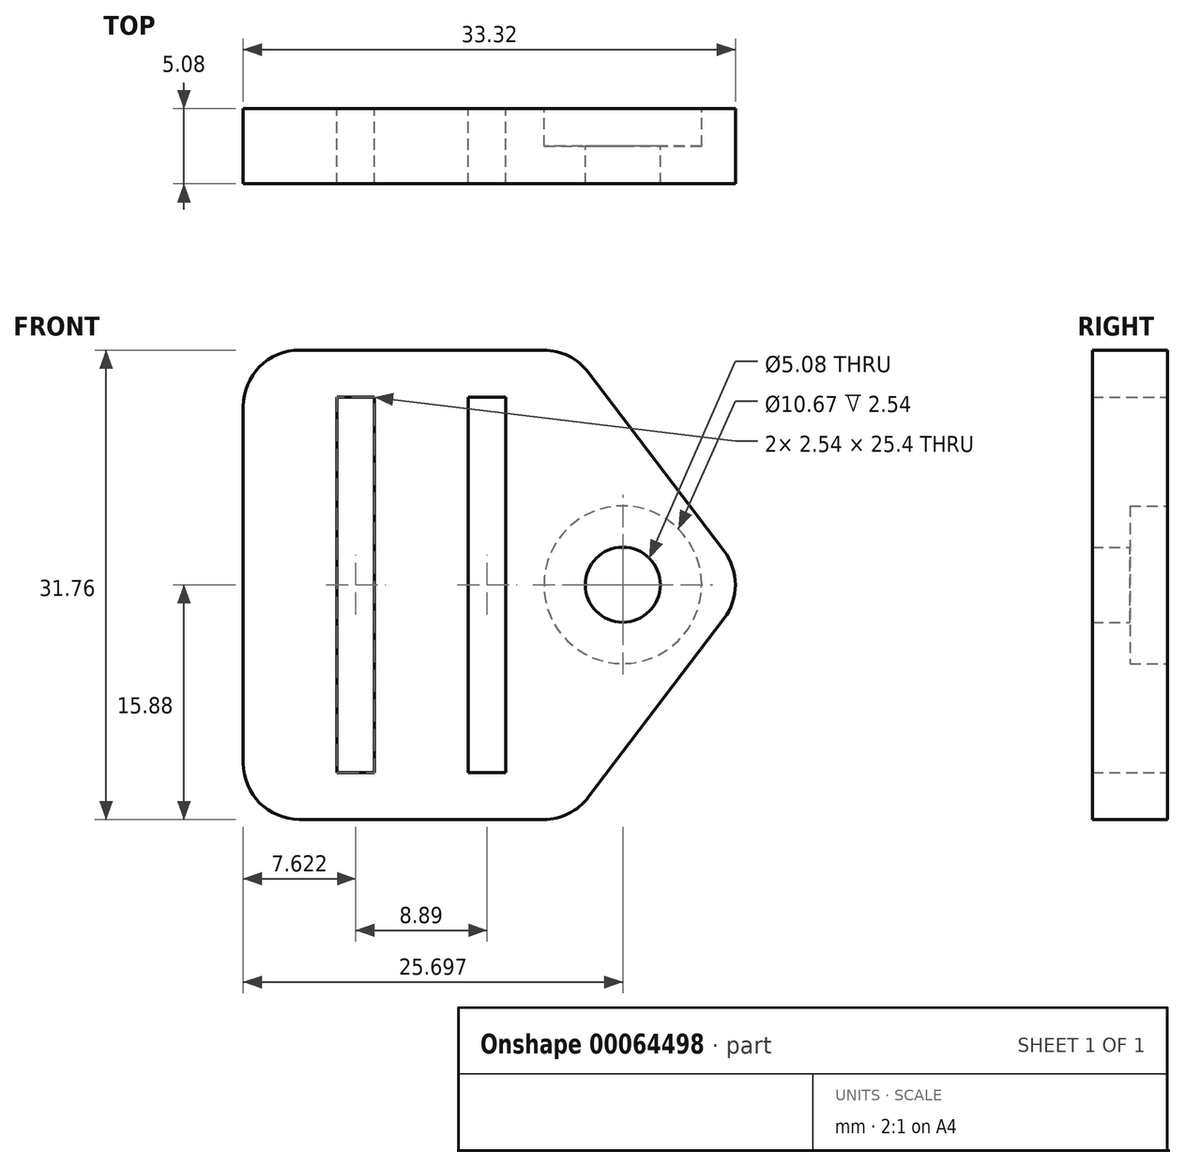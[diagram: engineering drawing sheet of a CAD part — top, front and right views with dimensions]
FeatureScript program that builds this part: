
annotation { "Feature Type Name" : "Feature", "Feature Type Description" : "" }
export const myFeature = defineFeature(function(context is Context, id is Id, definition is map)
    precondition{}
    {
        {
            var Q0;
            Q0=qCreatedBy(makeId("Front.planeOp"),FACE);
            var sketch = newSketch(context, id + "F0", { "sketchPlane" : qUnion([Q0])});
            skLineSegment(sketch, "E0", {"start": v(-37.2, 12.06) * mm, "end": v(-37.2, -12.07) * mm});
            skLineSegment(sketch, "E1", {"start": v(-33.4, -15.88) * mm, "end": v(-16.87, -15.88) * mm});
            skLineSegment(sketch, "E2", {"start": v(-13.84, -14.37) * mm, "end": v(-4.67, -2.3) * mm});
            skLineSegment(sketch, "E3", {"start": v(-4.67, 2.3) * mm, "end": v(-13.84, 14.37) * mm});
            skLineSegment(sketch, "E4", {"start": v(-16.87, 15.88) * mm, "end": v(-33.4, 15.88) * mm});
            skPoint(sketch, "E5.visualSharp", {"position": v(-37.2, 15.87) * mm});
            skArc(sketch, "E5.filletArc", {"start": v(-33.4, 15.87) * mm, "mid": v(-36.1, 14.76) * mm, "end": v(-37.2, 12.06) * mm});
            skPoint(sketch, "E6.visualSharp", {"position": v(-14.98, 15.88) * mm});
            skArc(sketch, "E6.filletArc", {"start": v(-13.84, 14.37) * mm, "mid": v(-15.18, 15.48) * mm, "end": v(-16.87, 15.88) * mm});
            skPoint(sketch, "E7.visualSharp", {"position": v(-37.2, -15.88) * mm});
            skArc(sketch, "E7.filletArc", {"start": v(-37.2, -12.07) * mm, "mid": v(-36.1, -14.76) * mm, "end": v(-33.4, -15.88) * mm});
            skPoint(sketch, "E8.visualSharp", {"position": v(-14.98, -15.88) * mm});
            skArc(sketch, "E8.filletArc", {"start": v(-16.87, -15.88) * mm, "mid": v(-15.18, -15.48) * mm, "end": v(-13.84, -14.37) * mm});
            skPoint(sketch, "E9.visualSharp", {"position": v(-2.92, 0) * mm});
            skArc(sketch, "E9.filletArc", {"start": v(-4.67, -2.3) * mm, "mid": v(-3.9, 0) * mm, "end": v(-4.67, 2.3) * mm});
            skLineSegment(sketch, "E10", {"start": v(-37.2, 0) * mm, "end": v(-2.92, 0) * mm});
            skLineSegment(sketch, "E11.bottom", {"start": v(-28.32, -12.7) * mm, "end": v(-30.86, -12.7) * mm});
            skLineSegment(sketch, "E11.top", {"start": v(-28.32, 12.7) * mm, "end": v(-30.86, 12.7) * mm});
            skLineSegment(sketch, "E11.left", {"start": v(-28.32, -12.7) * mm, "end": v(-28.32, 12.7) * mm});
            skLineSegment(sketch, "E11.right", {"start": v(-30.86, -12.7) * mm, "end": v(-30.86, 12.7) * mm});
            skPoint(sketch, "E11.middle", {"position": v(-29.59, 0) * mm});
            skLineSegment(sketch, "E12.bottom", {"start": v(-19.43, -12.7) * mm, "end": v(-21.97, -12.7) * mm});
            skLineSegment(sketch, "E12.top", {"start": v(-19.43, 12.7) * mm, "end": v(-21.97, 12.7) * mm});
            skLineSegment(sketch, "E12.left", {"start": v(-19.43, -12.7) * mm, "end": v(-19.43, 12.7) * mm});
            skLineSegment(sketch, "E12.right", {"start": v(-21.97, -12.7) * mm, "end": v(-21.97, 12.7) * mm});
            skPoint(sketch, "E12.middle", {"position": v(-20.7, 0) * mm});
            skCircle(sketch, "E13", {"center": v(-11.51, 0) * mm, "radius": 2.54 * mm});
            skSolve(sketch);
        }
        {
            var Q0;
            {var subQ1=sQuery(id+"F0.wireOp",EDGE,"E3");Q0=makeQuery(id+"F0.imprint","IMPRINT",FACE,{"disambiguationData":[TD([[makeQuery(id+"F0.imprint","IMPRINT",EDGE,{"derivedFrom":subQ1}),1.0]])]});}
            var Q1;
            Q1=makeQuery(id+"F0.imprint","IMPRINT",FACE,{"disambiguationData":[TD([[makeQuery(id+"F0.imprint","IMPRINT",EDGE,{"derivedFrom":sQuery(id+"F0.wireOp",EDGE,"E1")}),1.0]])]});
            extrude(context, id + "F1", {"entities" : qUnion([Q0, Q1]), "depth" : 5.08 * mm});
        }
        {
            var Q0;
            Q0=makeQuery(id+"F1.opExtrude","CAP_FACE",FACE,{"disambiguationData":[OSD([sQuery(id+"F0.wireOp",EDGE,"E0"),sQuery(id+"F0.wireOp",EDGE,"E1"),sQuery(id+"F0.wireOp",EDGE,"E2"),sQuery(id+"F0.wireOp",EDGE,"E3"),sQuery(id+"F0.wireOp",EDGE,"E4"),sQuery(id+"F0.wireOp",EDGE,"E5.filletArc"),sQuery(id+"F0.wireOp",EDGE,"E6.filletArc"),sQuery(id+"F0.wireOp",EDGE,"E7.filletArc"),sQuery(id+"F0.wireOp",EDGE,"E8.filletArc"),sQuery(id+"F0.wireOp",EDGE,"E9.filletArc"),sQuery(id+"F0.wireOp",EDGE,"E11.bottom"),sQuery(id+"F0.wireOp",EDGE,"E11.top"),sQuery(id+"F0.wireOp",EDGE,"E11.left"),sQuery(id+"F0.wireOp",EDGE,"E11.right"),sQuery(id+"F0.wireOp",EDGE,"E12.bottom"),sQuery(id+"F0.wireOp",EDGE,"E12.top"),sQuery(id+"F0.wireOp",EDGE,"E12.left"),sQuery(id+"F0.wireOp",EDGE,"E12.right"),sQuery(id+"F0.wireOp",EDGE,"E13")])],"isStart":true});
            var sketch = newSketch(context, id + "F2", { "sketchPlane" : qUnion([Q0])});
            skCircle(sketch, "E14", {"center": v(11.51, 0) * mm, "radius": 5.33 * mm});
            skSolve(sketch);
        }
        {
            var Q0;
            Q0=makeQuery(id+"F2.imprint","IMPRINT",FACE,{"disambiguationData":[TD([[makeQuery(id+"F2.imprint","IMPRINT",EDGE,{"derivedFrom":sQuery(id+"F2.wireOp",EDGE,"E14")}),1.0]])]});
            extrude(context, id + "F3", {"entities" : qUnion([Q0]), "operationType" : NewBodyOperationType.REMOVE, "oppositeDirection" : true, "depth" : 2.54 * mm});
        }
    });
